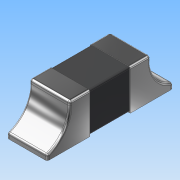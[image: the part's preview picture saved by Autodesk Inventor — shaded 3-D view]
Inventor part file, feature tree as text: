
AUTODESK INVENTOR PART (.ipt)
format: ipt  version: 2016 (Build 200138000, 138)  size: 203,264 bytes
history: native  units: mm
features: extrude x3, fillet x3, sketch x2, mirror x1, projected_geometry x1
ambient origin geometry x8: Origin, YZ Plane, XZ Plane, XY Plane, X Axis, Y Axis, Z Axis, Center Point
bodies: Body1 (feature_tree)
feature tree (10):
  extrude  "Extrusion4"  Depth=0.775mm
  sketch  "Sketch11"  dims[d9=0.775mm d10=0.0mm d11=0.8mm d12=0.4mm d13=0.0mm d14=0.1mm d15=0.85mm d16=0.0mm d17=0.65mm d18=0.0425mm d19=0.03mm]
  extrude  "Extrusion5"  Depth=0.8mm
  extrude  "Extrusion6"  Depth=0.4mm TaperAngle=0.0deg
  fillet  "Fillet1"  Radius=0.1mm
  fillet  "Fillet2"  Radius=0.85mm
  mirror  "Mirror1"
  fillet  "Fillet3"  Radius=0.65mm
  sketch  "Sketch10"  dims[d7=0.8mm d8=0.775mm]
  projected_geometry  "Projected Loop1"
